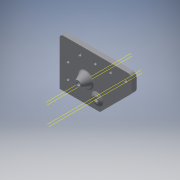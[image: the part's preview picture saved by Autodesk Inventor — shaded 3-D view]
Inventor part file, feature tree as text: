
AUTODESK INVENTOR PART (.ipt)
format: ipt  version: 2018 (Build 220112000, 112)  size: 211,968 bytes
history: native  units: in
note: dims shown in document units (in); Inventor stores cm internally (conversion verified against a paired STEP export)
features: sketch x8, extrude x6, plane x4, revolve x2, fillet x2, projected_geometry x2
ambient origin geometry x8: Origin, YZ Plane, XZ Plane, XY Plane, X Axis, Y Axis, Z Axis, Center Point
bodies: Solid1 (feature_tree)
feature tree (24):
  extrude  "Extrusion1"  Depth=0.7874in
  extrude  "Extrusion2"  Depth=3.5433in
  plane  "Work Plane2"
  revolve  "Revolution1"  [1 undecoded]
  extrude  "Extrusion3"  Depth=0.5512in
  extrude  "Extrusion4"  [1 undecoded]
  fillet  "Fillet1"  Radius=0.3543in
  extrude  "Extrusion5"  TaperAngle=90.0deg  [1 undecoded]
  plane  "Work Plane4"
  revolve  "Revolution2"  [1 undecoded]
  fillet  "Fillet2"  Radius=0.1654in
  extrude  "Extrusion6"  Depth=0.3937in
  sketch  "Sketch1"  dims[d0=0.7874in d1=0.7874in]
  sketch  "Sketch2"  dims[d2=3.5433in d3=3.5433in]
  plane  "Work Plane1"
  sketch  "Sketch3"  dims[d4=0.2362in d5=0.0in d6=0.1969in]
  sketch  "Sketch4"  dims[d7=1.2992in d8=0.5512in]
  projected_geometry  "Projected Loop1"
  sketch  "Sketch5"  dims[d9=0.2362in d10=0.0in d11=-0.0984in d12=0.3543in]
  sketch  "Sketch7"  dims[d13=0.3937in d14=90.0deg]
  plane  "Work Plane3"
  sketch  "Sketch8"  dims[d15=0.2362in d16=0.0in d17=0.1575in d18=0.1654in]
  projected_geometry  "Projected Loop2"
  sketch  "Sketch9"  dims[d19=0.315in d20=0.748in d21=0.748in d22=0.748in d23=0.315in d24=0.748in d25=0.748in d26=0.748in d27=0.2362in d28=0.0in d29=0.0787in d30=0.3543in d32=0.3543in d33=0.1969in d34=0.0in d35=0.0984in d36=0.1969in d37=0.0591in d38=0.0787in d39=90.0deg d40=0.1969in d42=0.3937in d43=0.0in d44=1.2598in]
note: 4 required parameter values undecoded (feature->parameter linkage not recoverable at this tier; creation-order binding heuristic only, values carry confidence <= 0.55)